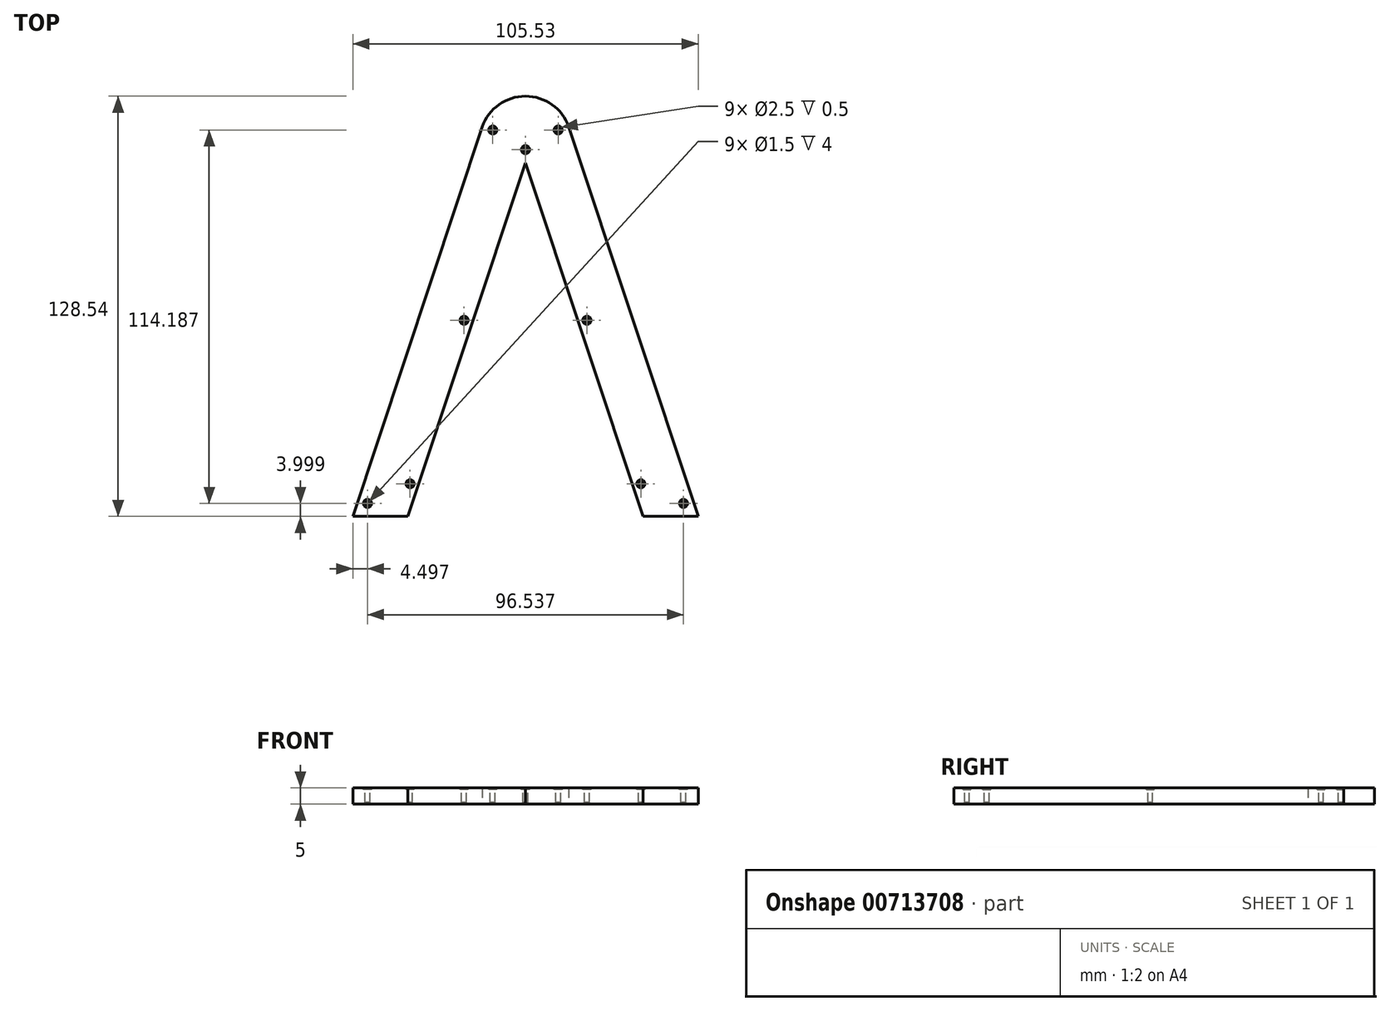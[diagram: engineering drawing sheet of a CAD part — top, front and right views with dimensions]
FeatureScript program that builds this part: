
annotation { "Feature Type Name" : "Feature", "Feature Type Description" : "" }
export const myFeature = defineFeature(function(context is Context, id is Id, definition is map)
    precondition{}
    {
        {
            var Q0;
            Q0=qCreatedBy(makeId("Top.planeOp"),FACE);
            var sketch = newSketch(context, id + "F0", { "sketchPlane" : qUnion([Q0])});
            skLineSegment(sketch, "E0.0", {"start": v(-65.22, -41.8) * mm, "end": v(-101.12, -149.98) * mm});
            skLineSegment(sketch, "E1.0", {"start": v(-65.22, -41.8) * mm, "end": v(-29.3, -149.98) * mm});
            skPoint(sketch, "E2", {"position": v(-65.22, -41.8) * mm});
            skPoint(sketch, "E3", {"position": v(-101.12, -149.98) * mm});
            skPoint(sketch, "E4", {"position": v(-29.3, -149.98) * mm});
            skArc(sketch, "E5.0", {"start": v(-78.43, -30.82) * mm, "mid": v(-65.22, -21.44) * mm, "end": v(-52, -30.82) * mm});
            skLineSegment(sketch, "E5.1", {"start": v(-78.43, -30.82) * mm, "end": v(-117.98, -149.98) * mm});
            skLineSegment(sketch, "E5.2", {"start": v(-117.98, -149.98) * mm, "end": v(-101.12, -149.98) * mm});
            skLineSegment(sketch, "E5.3", {"start": v(-52, -30.82) * mm, "end": v(-12.45, -149.98) * mm});
            skLineSegment(sketch, "E6.trimOffspring", {"start": v(-29.3, -149.98) * mm, "end": v(-12.45, -149.98) * mm});
            skSolve(sketch);
        }
        {
            var Q0;
            Q0 = qSketchRegion(id + "F0", true);
            extrude(context, id + "F1", {"entities" : qUnion([Q0]), "depth" : 5 * mm, "offsetDistance" : 25 * mm});
        }
        {
            var Q0;
            Q0=makeQuery(id+"F1.opExtrude","CAP_FACE",FACE,{"disambiguationData":[OSD([sQuery(id+"F0.wireOp",EDGE,"E0.0"),sQuery(id+"F0.wireOp",EDGE,"E1.0"),sQuery(id+"F0.wireOp",EDGE,"E5.0"),sQuery(id+"F0.wireOp",EDGE,"E5.1"),sQuery(id+"F0.wireOp",EDGE,"E5.2"),sQuery(id+"F0.wireOp",EDGE,"E5.3"),sQuery(id+"F0.wireOp",EDGE,"E6.trimOffspring")])],"isStart":false});
            var sketch = newSketch(context, id + "F2", { "sketchPlane" : qUnion([Q0])});
            skCircle(sketch, "E7", {"center": v(-65.22, -37.8) * mm, "radius": 0.75 * mm});
            skCircle(sketch, "E8", {"center": v(-113.48, -145.98) * mm, "radius": 0.75 * mm});
            skCircle(sketch, "E9", {"center": v(-100.48, -139.98) * mm, "radius": 0.75 * mm});
            skCircle(sketch, "E10", {"center": v(-29.95, -139.98) * mm, "radius": 0.75 * mm});
            skCircle(sketch, "E11", {"center": v(-16.95, -145.98) * mm, "radius": 0.75 * mm});
            skCircle(sketch, "E12", {"center": v(-83.98, -89.98) * mm, "radius": 0.75 * mm});
            skCircle(sketch, "E13", {"center": v(-46.45, -89.98) * mm, "radius": 0.75 * mm});
            skCircle(sketch, "E14", {"center": v(-75.22, -31.8) * mm, "radius": 0.75 * mm});
            skCircle(sketch, "E15", {"center": v(-55.22, -31.8) * mm, "radius": 0.75 * mm});
            skSolve(sketch);
        }
        {
            var Q0;
            Q0 = qSketchRegion(id + "F2", true);
            extrude(context, id + "F3", {"entities" : qUnion([Q0]), "operationType" : NewBodyOperationType.REMOVE, "oppositeDirection" : true, "depth" : 4.5 * mm, "offsetDistance" : 25 * mm});
        }
        {
            var Q0;
            Q0=makeQuery(id+"F1.opExtrude","CAP_FACE",FACE,{"disambiguationData":[OSD([sQuery(id+"F0.wireOp",EDGE,"E0.0"),sQuery(id+"F0.wireOp",EDGE,"E1.0"),sQuery(id+"F0.wireOp",EDGE,"E5.0"),sQuery(id+"F0.wireOp",EDGE,"E5.1"),sQuery(id+"F0.wireOp",EDGE,"E5.2"),sQuery(id+"F0.wireOp",EDGE,"E5.3"),sQuery(id+"F0.wireOp",EDGE,"E6.trimOffspring")])],"isStart":false});
            var sketch = newSketch(context, id + "F4", { "sketchPlane" : qUnion([Q0])});
            skCircle(sketch, "E16", {"center": v(-75.22, -31.8) * mm, "radius": 1.25 * mm});
            skCircle(sketch, "E17", {"center": v(-65.22, -37.8) * mm, "radius": 1.25 * mm});
            skCircle(sketch, "E18", {"center": v(-55.22, -31.8) * mm, "radius": 1.25 * mm});
            skCircle(sketch, "E19", {"center": v(-46.45, -89.98) * mm, "radius": 1.25 * mm});
            skCircle(sketch, "E20", {"center": v(-83.98, -89.98) * mm, "radius": 1.25 * mm});
            skCircle(sketch, "E21", {"center": v(-16.95, -145.98) * mm, "radius": 1.25 * mm});
            skCircle(sketch, "E22", {"center": v(-29.95, -139.98) * mm, "radius": 1.25 * mm});
            skCircle(sketch, "E23", {"center": v(-100.48, -139.98) * mm, "radius": 1.25 * mm});
            skCircle(sketch, "E24", {"center": v(-113.48, -145.98) * mm, "radius": 1.25 * mm});
            skSolve(sketch);
        }
        {
            var Q0;
            Q0 = qSketchRegion(id + "F4", true);
            extrude(context, id + "F5", {"entities" : qUnion([Q0]), "operationType" : NewBodyOperationType.REMOVE, "oppositeDirection" : true, "depth" : 0.5 * mm, "offsetDistance" : 25 * mm});
        }
    });
